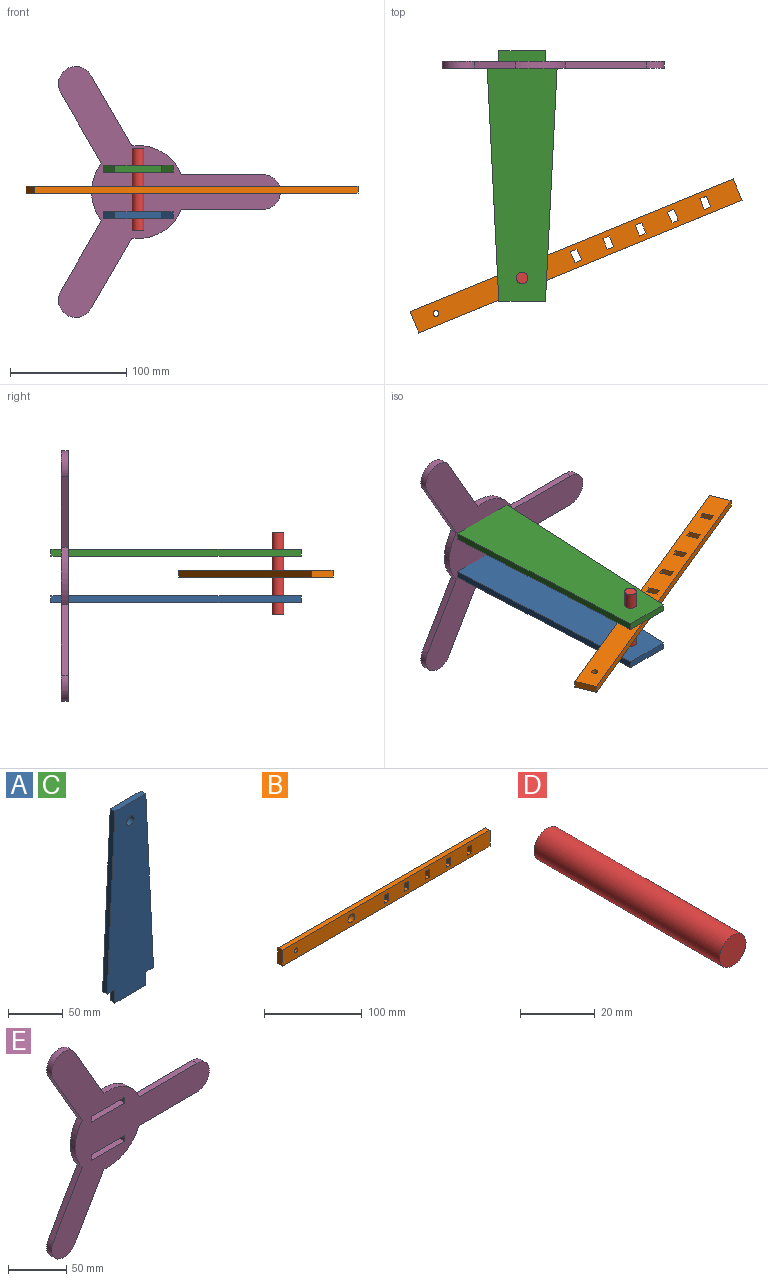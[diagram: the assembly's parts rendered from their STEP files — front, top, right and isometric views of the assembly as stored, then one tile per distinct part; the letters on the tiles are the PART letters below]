
ASSEMBLY  parts=5 mates=8
PART A: 11 faces, bbox 60x6x215 mm
  f0: plane 10x6mm, normal (0,0,-1), area 60mm2, adj f1,f8,f9,f10
  f1: plane 15x6mm, normal (-1,0,0), area 90mm2, adj f0,f2,f9,f10
  f2: plane 40x6mm, normal (0,0,-1), area 240mm2, adj f1,f3,f9,f10
  f3: plane 15x6mm, normal (1,0,0), area 90mm2, adj f2,f4,f9,f10
  f4: plane 10x6mm, normal (0,0,-1), area 60mm2, adj f3,f5,f9,f10
  f5: plane 200x10mm, normal (1,0,0.05), area 1201.5mm2, adj f4,f6,f9,f10
  f6: plane 40x6mm, normal (0,0,1), area 240mm2, adj f5,f8,f9,f10
  f7: cylinder r=5mm len=10mm, axis (0,1,0), area 188.5mm2, adj f9,f10
  f8: plane 200x10mm, normal (-1,0,0.05), area 1201.5mm2, adj f0,f6,f9,f10
  f9: plane 215x60mm, normal (0,-1,0), area 10521.5mm2, adj f0,f1,f2,f3,f4,f5,f6,f7
  f10: plane 215x60mm, normal (0,1,0), area 10521.5mm2, adj f0,f1,f2,f3,f4,f5,f6,f7
PART B: 28 faces, bbox 300x6x20 mm
  f0: plane 300x6mm, normal (0,0,-1), area 1800mm2, adj f1,f25,f26,f27
  f1: plane 20x6mm, normal (1,0,0), area 120mm2, adj f0,f2,f26,f27
  f2: plane 300x6mm, normal (0,0,1), area 1800mm2, adj f1,f25,f26,f27
  f3: plane 10x6mm, normal (-1,0,0), area 60mm2, adj f4,f18,f26,f27
  f4: plane 6x6mm, normal (0,0,1), area 36mm2, adj f3,f5,f26,f27
  f5: plane 10x6mm, normal (1,0,0), area 60mm2, adj f4,f18,f26,f27
  f6: plane 10x6mm, normal (-1,0,0), area 60mm2, adj f7,f21,f26,f27
  f7: plane 6x6mm, normal (0,0,1), area 36mm2, adj f6,f8,f26,f27
  f8: plane 10x6mm, normal (1,0,0), area 60mm2, adj f7,f21,f26,f27
  f9: plane 10x6mm, normal (-1,0,0), area 60mm2, adj f10,f22,f26,f27
  f10: plane 6x6mm, normal (0,0,1), area 36mm2, adj f9,f11,f26,f27
  f11: plane 10x6mm, normal (1,0,0), area 60mm2, adj f10,f22,f26,f27
  f12: plane 10x6mm, normal (-1,0,0), area 60mm2, adj f13,f23,f26,f27
  f13: plane 6x6mm, normal (0,0,1), area 36mm2, adj f12,f14,f26,f27
  f14: plane 10x6mm, normal (1,0,0), area 60mm2, adj f13,f23,f26,f27
  f15: plane 10x6mm, normal (-1,0,0), area 60mm2, adj f16,f24,f26,f27
  f16: plane 6x6mm, normal (0,0,1), area 36mm2, adj f15,f17,f26,f27
  f17: plane 10x6mm, normal (1,0,0), area 60mm2, adj f16,f24,f26,f27
  f18: plane 6x6mm, normal (0,0,-1), area 36mm2, adj f3,f5,f26,f27
  f19: cylinder r=5mm len=10mm, axis (0,1,0), area 188.5mm2, adj f26,f27
  f20: cylinder r=2.5mm len=6mm, axis (0,1,0), area 94.2mm2, adj f26,f27
  f21: plane 6x6mm, normal (0,0,-1), area 36mm2, adj f6,f8,f26,f27
  f22: plane 6x6mm, normal (0,0,-1), area 36mm2, adj f9,f11,f26,f27
  f23: plane 6x6mm, normal (0,0,-1), area 36mm2, adj f12,f14,f26,f27
  f24: plane 6x6mm, normal (0,0,-1), area 36mm2, adj f15,f17,f26,f27
  f25: plane 20x6mm, normal (-1,0,0), area 120mm2, adj f0,f2,f26,f27
  f26: plane 300x20mm, normal (0,-1,0), area 5601.8mm2, adj f0,f1,f2,f3,f4,f5,f6,f7
  f27: plane 300x20mm, normal (0,1,0), area 5601.8mm2, adj f0,f1,f2,f3,f4,f5,f6,f7
PART C: same geometry as A
PART D: 3 faces, bbox 10x70x10 mm
  f0: cylinder r=5mm len=70mm, axis (0,1,0), area 2199.1mm2, adj f1,f2
  f1: plane 10x10mm, normal (0,-1,0), area 78.5mm2, adj f0
  f2: plane 10x10mm, normal (0,1,0), area 78.5mm2, adj f0
PART E: 22 faces, bbox 190.6x6x215.5 mm
  f0: cylinder r=40mm len=49.23mm, axis (0,1,0), area 318.1mm2, adj f1,f19,f20,f21
  f1: plane 60.62x35mm, normal (-0.87,0,0.5), area 420mm2, adj f0,f2,f20,f21
  f2: cylinder r=15mm len=27.99mm, axis (0,1,0), area 282.7mm2, adj f1,f3,f20,f21
  f3: plane 60.62x35mm, normal (0.87,0,-0.5), area 420mm2, adj f2,f4,f20,f21
  f4: cylinder r=40mm len=42.63mm, axis (0,1,0), area 318.1mm2, adj f3,f5,f20,f21
  f5: plane 70x6mm, normal (0,0,-1), area 420mm2, adj f4,f6,f20,f21
  f6: cylinder r=15mm len=30mm, axis (0,1,0), area 282.7mm2, adj f5,f7,f20,f21
  f7: plane 70x6mm, normal (0,0,1), area 420mm2, adj f6,f8,f20,f21
  f8: cylinder r=40mm len=42.63mm, axis (0,1,0), area 318.1mm2, adj f7,f9,f20,f21
  f9: plane 60.62x35mm, normal (0.87,0,0.5), area 420mm2, adj f8,f10,f20,f21
  f10: cylinder r=15mm len=27.99mm, axis (0,1,0), area 282.7mm2, adj f9,f19,f20,f21
  f11: plane 40x6mm, normal (0,0,-1), area 240mm2, adj f12,f17,f20,f21
  f12: plane 6x6mm, normal (-1,0,0), area 36mm2, adj f11,f13,f20,f21
  f13: plane 40x6mm, normal (0,0,1), area 240mm2, adj f12,f17,f20,f21
  f14: plane 6x6mm, normal (-1,0,0), area 36mm2, adj f15,f18,f20,f21
  f15: plane 40x6mm, normal (0,0,1), area 240mm2, adj f14,f16,f20,f21
  f16: plane 6x6mm, normal (1,0,0), area 36mm2, adj f15,f18,f20,f21
  f17: plane 6x6mm, normal (1,0,0), area 36mm2, adj f11,f13,f20,f21
  f18: plane 40x6mm, normal (0,0,-1), area 240mm2, adj f14,f16,f20,f21
  f19: plane 60.62x35mm, normal (-0.87,0,-0.5), area 420mm2, adj f0,f10,f20,f21
  f20: plane 215.47x190.62mm, normal (0,-1,0), area 11730.4mm2, adj f0,f1,f2,f3,f4,f5,f6,f7
  f21: plane 215.47x190.62mm, normal (0,1,0), area 11730.4mm2, adj f0,f1,f2,f3,f4,f5,f6,f7
PLACE A rot(axis=(1,0,0),90deg) t=(0,1.5,-17)mm
PLACE B rot(axis=(-0.96,-0.19,0.19),92.1deg) t=(46.25,-167,-1)mm
PLACE C rot(axis=(1,0,0),90deg) t=(0,1.5,23)mm
PLACE D rot(axis=(1,0,0),90deg) t=(0,-186,37)mm
PLACE E at identity fixed
MATE fastened D.f0 <-> A.f7  axis (0,0,-1) through (0,-186,-33)mm
MATE planar C.f4 <-> E.f8  axis (0,1,0) through (25,-6,20)mm
MATE cylindrical A.f2 <-> E.f20  axis (0,1,0) through (20,9,-17)mm
MATE planar A.f4 <-> E.f8  axis (0,1,0) through (25,-6,-20)mm
MATE cylindrical A.f2 <-> E.f20  axis (0,1,0) through (-20,9,-23)mm
MATE revolute B.f19 <-> D.f0  axis (0,0,-1) through (0,-186,2)mm
MATE cylindrical C.f2 <-> E.f20  axis (0,1,0) through (-20,9,17)mm
MATE cylindrical C.f2 <-> E.f20  axis (0,1,0) through (20,9,23)mm
